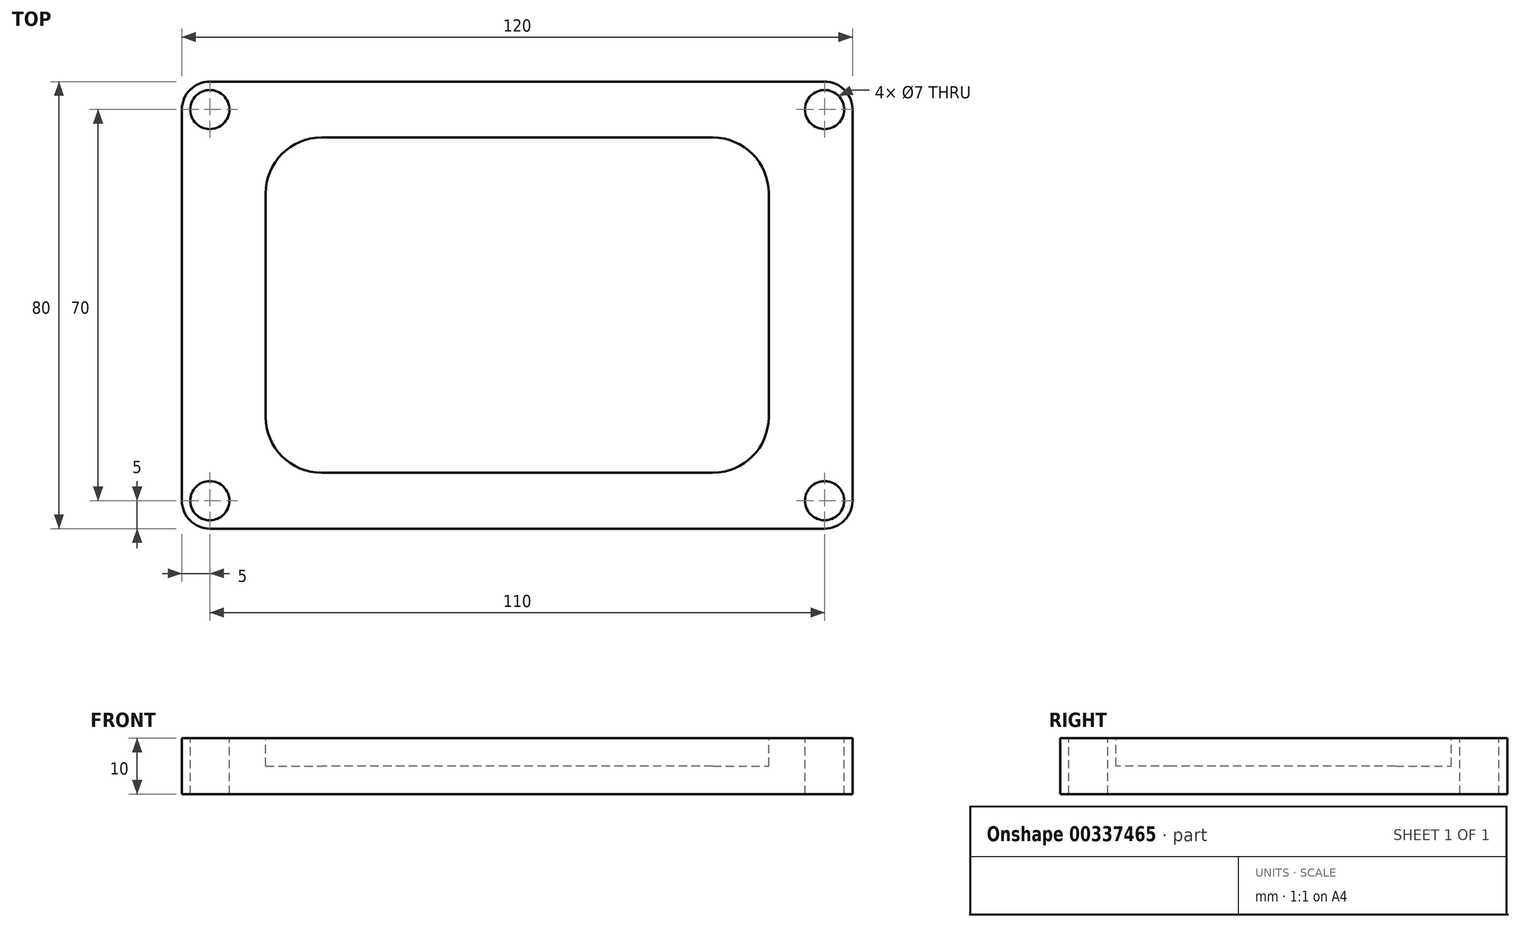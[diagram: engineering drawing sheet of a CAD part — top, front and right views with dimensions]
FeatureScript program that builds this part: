
annotation { "Feature Type Name" : "Feature", "Feature Type Description" : "" }
export const myFeature = defineFeature(function(context is Context, id is Id, definition is map)
    precondition{}
    {
        {
            var Q0;
            Q0=qCreatedBy(makeId("Top.planeOp"),FACE);
            var sketch = newSketch(context, id + "F0", { "sketchPlane" : qUnion([Q0])});
            skLineSegment(sketch, "E0.bottom", {"start": v(60, 40) * mm, "end": v(-60, 40) * mm});
            skLineSegment(sketch, "E0.top", {"start": v(60, -40) * mm, "end": v(-60, -40) * mm});
            skLineSegment(sketch, "E0.left", {"start": v(60, 40) * mm, "end": v(60, -40) * mm});
            skLineSegment(sketch, "E0.right", {"start": v(-60, 40) * mm, "end": v(-60, -40) * mm});
            skPoint(sketch, "E0.middle", {"position": v(0, 0) * mm});
            skSolve(sketch);
        }
        {
            var Q0;
            Q0=makeQuery(id+"F0.imprint","IMPRINT",FACE,{"disambiguationData":[TD([[makeQuery(id+"F0.imprint","IMPRINT",EDGE,{"derivedFrom":sQuery(id+"F0.wireOp",EDGE,"E0.bottom")}),1.0]])]});
            extrude(context, id + "F1", {"entities" : qUnion([Q0]), "depth" : 10 * mm});
        }
        {
            var Q0;
            Q0=makeQuery(id+"F1.opExtrude","SWEPT_EDGE",EDGE,{"disambiguationData":[OSD([sQuery(id+"F0.wireOp",EDGE,"E0.top"),sQuery(id+"F0.wireOp",EDGE,"E0.left")])]});
            var Q1;
            Q1=makeQuery(id+"F1.opExtrude","SWEPT_EDGE",EDGE,{"disambiguationData":[OSD([sQuery(id+"F0.wireOp",EDGE,"E0.bottom"),sQuery(id+"F0.wireOp",EDGE,"E0.left")])]});
            var Q2;
            Q2=makeQuery(id+"F1.opExtrude","SWEPT_EDGE",EDGE,{"disambiguationData":[OSD([sQuery(id+"F0.wireOp",EDGE,"E0.top"),sQuery(id+"F0.wireOp",EDGE,"E0.right")])]});
            var Q3;
            Q3=makeQuery(id+"F1.opExtrude","SWEPT_EDGE",EDGE,{"disambiguationData":[OSD([sQuery(id+"F0.wireOp",EDGE,"E0.bottom"),sQuery(id+"F0.wireOp",EDGE,"E0.right")])]});
            fillet(context, id + "F2", {"entities" : qUnion([Q0, Q1, Q2, Q3]), "radius" : 5 * mm, "tangentPropagation" : true, "allowEdgeOverflow" : false});
        }
        {
            var Q0;
            Q0=makeQuery(id+"F1.opExtrude","CAP_FACE",FACE,{"disambiguationData":[OSD([sQuery(id+"F0.wireOp",EDGE,"E0.bottom"),sQuery(id+"F0.wireOp",EDGE,"E0.top"),sQuery(id+"F0.wireOp",EDGE,"E0.left"),sQuery(id+"F0.wireOp",EDGE,"E0.right")])],"isStart":false});
            var sketch = newSketch(context, id + "F3", { "sketchPlane" : qUnion([Q0])});
            skLineSegment(sketch, "E1.bottom", {"start": v(45, 30) * mm, "end": v(-45, 30) * mm});
            skLineSegment(sketch, "E1.top", {"start": v(45, -30) * mm, "end": v(-45, -30) * mm});
            skLineSegment(sketch, "E1.left", {"start": v(45, 30) * mm, "end": v(45, -30) * mm});
            skLineSegment(sketch, "E1.right", {"start": v(-45, 30) * mm, "end": v(-45, -30) * mm});
            skPoint(sketch, "E1.middle", {"position": v(0, 0) * mm});
            skSolve(sketch);
        }
        {
            var Q0;
            Q0=makeQuery(id+"F3.imprint","IMPRINT",FACE,{"disambiguationData":[TD([[makeQuery(id+"F3.imprint","IMPRINT",EDGE,{"derivedFrom":sQuery(id+"F3.wireOp",EDGE,"E1.bottom")}),1.0]])]});
            extrude(context, id + "F4", {"entities" : qUnion([Q0]), "operationType" : NewBodyOperationType.REMOVE, "oppositeDirection" : true, "depth" : 5 * mm});
        }
        {
            var Q0;
            Q0=makeQuery(id+"F4.boolean.opBoolean","COPY",EDGE,{"derivedFrom":makeQuery(id+"F4.opExtrude","SWEPT_EDGE",EDGE,{"disambiguationData":[OSD([sQuery(id+"F3.wireOp",EDGE,"E1.bottom"),sQuery(id+"F3.wireOp",EDGE,"E1.right")])]})});
            var Q1;
            Q1=makeQuery(id+"F4.boolean.opBoolean","COPY",EDGE,{"derivedFrom":makeQuery(id+"F4.opExtrude","SWEPT_EDGE",EDGE,{"disambiguationData":[OSD([sQuery(id+"F3.wireOp",EDGE,"E1.bottom"),sQuery(id+"F3.wireOp",EDGE,"E1.left")])]})});
            var Q2;
            Q2=makeQuery(id+"F4.boolean.opBoolean","COPY",EDGE,{"derivedFrom":makeQuery(id+"F4.opExtrude","SWEPT_EDGE",EDGE,{"disambiguationData":[OSD([sQuery(id+"F3.wireOp",EDGE,"E1.top"),sQuery(id+"F3.wireOp",EDGE,"E1.left")])]})});
            var Q3;
            Q3=makeQuery(id+"F4.boolean.opBoolean","COPY",EDGE,{"derivedFrom":makeQuery(id+"F4.opExtrude","SWEPT_EDGE",EDGE,{"disambiguationData":[OSD([sQuery(id+"F3.wireOp",EDGE,"E1.top"),sQuery(id+"F3.wireOp",EDGE,"E1.right")])]})});
            fillet(context, id + "F5", {"entities" : qUnion([Q0, Q1, Q2, Q3]), "radius" : 10 * mm, "tangentPropagation" : true, "allowEdgeOverflow" : false});
        }
        {
            var Q0;
            Q0=makeQuery(id+"F1.opExtrude","CAP_FACE",FACE,{"disambiguationData":[OSD([sQuery(id+"F0.wireOp",EDGE,"E0.bottom"),sQuery(id+"F0.wireOp",EDGE,"E0.top"),sQuery(id+"F0.wireOp",EDGE,"E0.left"),sQuery(id+"F0.wireOp",EDGE,"E0.right")])],"isStart":false});
            var sketch = newSketch(context, id + "F6", { "sketchPlane" : qUnion([Q0])});
            skPoint(sketch, "E2", {"position": v(-55, -35) * mm});
            skPoint(sketch, "E3", {"position": v(55, -35) * mm});
            skPoint(sketch, "E4", {"position": v(55, 35) * mm});
            skPoint(sketch, "E5", {"position": v(-55, 35) * mm});
            skSolve(sketch);
        }
        {
            var Q0;
            Q0=sQuery(id+"F6.wireOp",VERTEX,"E2");
            var Q1;
            Q1=sQuery(id+"F6.wireOp",VERTEX,"E5");
            var Q2;
            Q2=sQuery(id+"F6.wireOp",VERTEX,"E3");
            var Q3;
            Q3=sQuery(id+"F6.wireOp",VERTEX,"E4");
            var Q4;
            Q4=makeQuery(id+"F1.opExtrude","SWEPT_BODY",BODY,{"disambiguationData":[OSD([sQuery(id+"F0.wireOp",EDGE,"E0.bottom"),sQuery(id+"F0.wireOp",EDGE,"E0.top"),sQuery(id+"F0.wireOp",EDGE,"E0.left"),sQuery(id+"F0.wireOp",EDGE,"E0.right")])]});
            hole(context, id + "F7", {"style" : HoleStyle.SIMPLE, "endStyle" : HoleEndStyle.THROUGH, "standardTappedOrClearance" : lookupTablePath({ "standard" : "ISO", "engagement" : "75%", "pitch" : "1 mm", "size" : "M8", "type" : "Tapped" }), "standardBlindInLast" : lookupTablePath({ "standard" : "ISO", "engagement" : "75%", "pitch" : "1 mm", "size" : "M8", "type" : "Tapped" }), "holeDiameter" : 7 * mm, "showTappedDepth" : true, "tappedDepth" : 12 * mm, "tapClearance" : 3, "locations" : qUnion([Q0, Q1, Q2, Q3]), "scope" : qUnion([Q4]), "majorDiameter" : 8 * mm});
        }
    });
